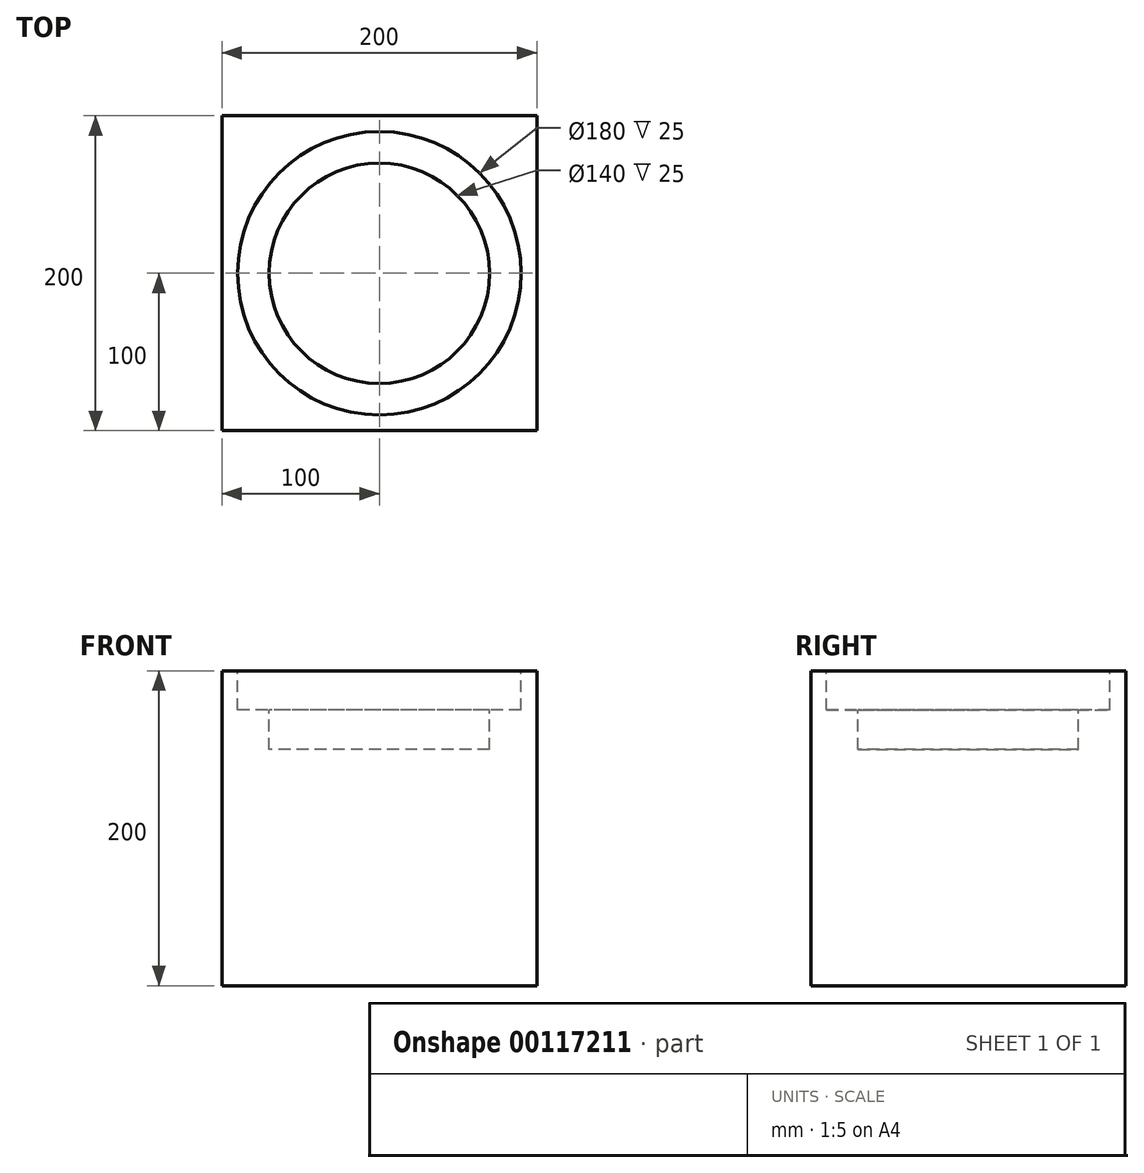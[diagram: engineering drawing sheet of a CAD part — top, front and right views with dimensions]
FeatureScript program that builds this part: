
annotation { "Feature Type Name" : "Feature", "Feature Type Description" : "" }
export const myFeature = defineFeature(function(context is Context, id is Id, definition is map)
    precondition{}
    {
        {
            var Q0;
            Q0=qCreatedBy(makeId("Front.planeOp"),FACE);
            var sketch = newSketch(context, id + "F0", { "sketchPlane" : qUnion([Q0])});
            skLineSegment(sketch, "E0.bottom", {"start": v(-100, -100) * mm, "end": v(100, -100) * mm});
            skLineSegment(sketch, "E0.top", {"start": v(-100, 100) * mm, "end": v(100, 100) * mm});
            skLineSegment(sketch, "E0.left", {"start": v(-100, -100) * mm, "end": v(-100, 100) * mm});
            skLineSegment(sketch, "E0.right", {"start": v(100, -100) * mm, "end": v(100, 100) * mm});
            skSolve(sketch);
        }
        {
            var Q0;
            Q0 = qSketchRegion(id + "F0", true);
            extrude(context, id + "F1", {"entities" : qUnion([Q0]), "endBound" : BoundingType.SYMMETRIC, "depth" : 200 * mm});
        }
        {
            var Q0;
            Q0=makeQuery(id+"F1.opExtrude","SWEPT_FACE",FACE,{"disambiguationData":[OSD([sQuery(id+"F0.wireOp",EDGE,"E0.top")])]});
            var sketch = newSketch(context, id + "F2", { "sketchPlane" : qUnion([Q0])});
            skCircle(sketch, "E1", {"center": v(0, 0) * mm, "radius": 90 * mm});
            skSolve(sketch);
        }
        {
            var Q0;
            Q0 = qSketchRegion(id + "F2", true);
            extrude(context, id + "F3", {"entities" : qUnion([Q0]), "operationType" : NewBodyOperationType.REMOVE, "oppositeDirection" : true, "depth" : 25 * mm});
        }
        {
            var Q0;
            Q0=makeQuery(id+"F3.boolean.opBoolean","COPY",FACE,{"derivedFrom":makeQuery(id+"F3.opExtrude","CAP_FACE",FACE,{"disambiguationData":[OSD([sQuery(id+"F2.wireOp",EDGE,"E1")])],"isStart":false})});
            var sketch = newSketch(context, id + "F4", { "sketchPlane" : qUnion([Q0])});
            skCircle(sketch, "E2", {"center": v(0, 0) * mm, "radius": 70 * mm});
            skSolve(sketch);
        }
        {
            var Q0;
            Q0 = qSketchRegion(id + "F4", true);
            extrude(context, id + "F5", {"entities" : qUnion([Q0]), "operationType" : NewBodyOperationType.REMOVE, "oppositeDirection" : true, "depth" : 25 * mm});
        }
    });
